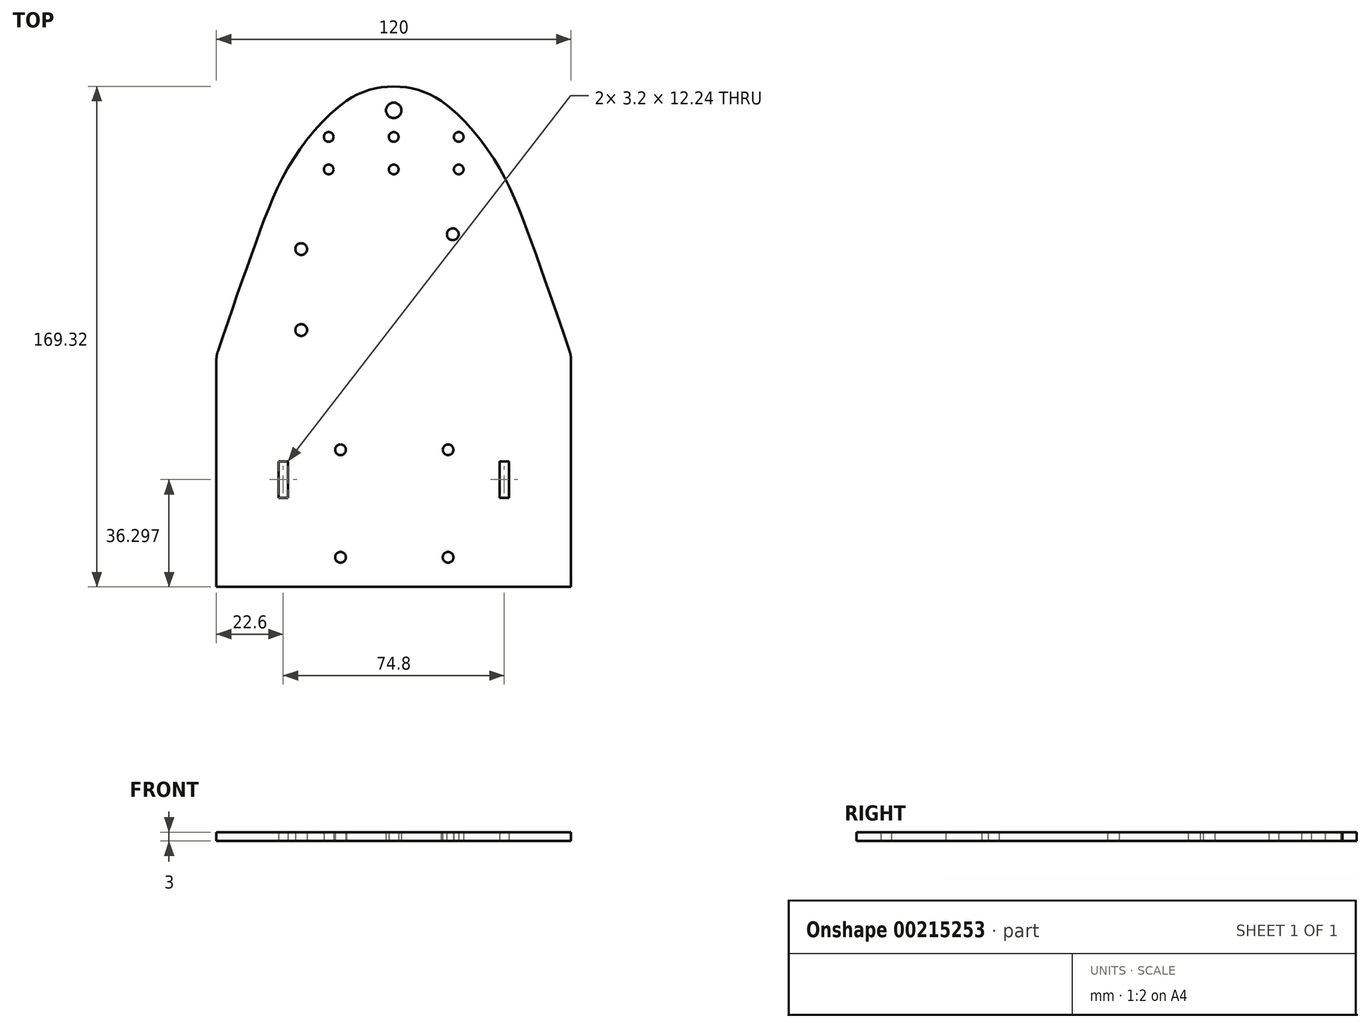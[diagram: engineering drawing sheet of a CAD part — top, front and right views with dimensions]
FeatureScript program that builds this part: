
annotation { "Feature Type Name" : "Feature", "Feature Type Description" : "" }
export const myFeature = defineFeature(function(context is Context, id is Id, definition is map)
    precondition{}
    {
        {
            var Q0;
            Q0=qCreatedBy(makeId("Top.planeOp"),FACE);
            var sketch = newSketch(context, id + "F0", { "sketchPlane" : qUnion([Q0])});
            skLineSegment(sketch, "E0", {"start": v(-69.46, 31.93) * mm, "end": v(50.54, 31.93) * mm, "construction": true});
            skLineSegment(sketch, "E1.bottom", {"start": v(-48.46, 5.05) * mm, "end": v(-45.26, 5.05) * mm});
            skLineSegment(sketch, "E1.top", {"start": v(-48.46, -7.2) * mm, "end": v(-45.26, -7.2) * mm});
            skLineSegment(sketch, "E1.left", {"start": v(-48.46, 5.05) * mm, "end": v(-48.46, -7.2) * mm});
            skLineSegment(sketch, "E1.right", {"start": v(-45.26, 5.05) * mm, "end": v(-45.26, -7.2) * mm});
            skLineSegment(sketch, "E2", {"start": v(-45.26, -1.07) * mm, "end": v(-45.26, -34.07) * mm, "construction": true});
            skLineSegment(sketch, "E3.top", {"start": v(-69.46, -37.37) * mm, "end": v(50.54, -37.37) * mm});
            skLineSegment(sketch, "E3.left", {"start": v(-69.46, 39.35) * mm, "end": v(-69.46, -37.37) * mm});
            skLineSegment(sketch, "E3.right", {"start": v(50.54, 39.35) * mm, "end": v(50.54, -37.37) * mm});
            skLineSegment(sketch, "E4", {"start": v(-45.26, -1.07) * mm, "end": v(-45.26, 31.93) * mm, "construction": true});
            skCircle(sketch, "E5", {"center": v(-27.46, -27.37) * mm, "radius": 1.82 * mm});
            skLineSegment(sketch, "E6", {"start": v(-27.46, -27.37) * mm, "end": v(8.94, -27.37) * mm, "construction": true});
            skCircle(sketch, "E7", {"center": v(8.94, -27.37) * mm, "radius": 1.82 * mm});
            skLineSegment(sketch, "E8", {"start": v(-27.46, -27.37) * mm, "end": v(-27.46, 9.03) * mm, "construction": true});
            skCircle(sketch, "E9", {"center": v(-27.46, 9.03) * mm, "radius": 1.82 * mm});
            skLineSegment(sketch, "E10", {"start": v(-27.46, 9.03) * mm, "end": v(8.94, 9.03) * mm, "construction": true});
            skCircle(sketch, "E11", {"center": v(8.94, 9.03) * mm, "radius": 1.8 * mm});
            skLineSegment(sketch, "E12", {"start": v(-40.76, 81.93) * mm, "end": v(10.54, 81.93) * mm, "construction": true});
            skLineSegment(sketch, "E13", {"start": v(10.54, 81.93) * mm, "end": v(10.54, 76.93) * mm, "construction": true});
            skCircle(sketch, "E14", {"center": v(10.54, 81.93) * mm, "radius": 2 * mm});
            skCircle(sketch, "E15", {"center": v(-40.76, 76.93) * mm, "radius": 2 * mm});
            skLineSegment(sketch, "E16", {"start": v(-40.76, 76.93) * mm, "end": v(-40.76, 49.53) * mm, "construction": true});
            skCircle(sketch, "E17", {"center": v(-40.76, 49.53) * mm, "radius": 2 * mm});
            skLineSegment(sketch, "E18", {"start": v(-40.76, 76.93) * mm, "end": v(-40.76, 81.93) * mm, "construction": true});
            skLineSegment(sketch, "E19", {"start": v(-9.46, -37.37) * mm, "end": v(-9.46, -58.96) * mm, "construction": true});
            skLineSegment(sketch, "E20.MirrorCS", {"start": v(29.54, 5.05) * mm, "end": v(29.54, -7.2) * mm});
            skLineSegment(sketch, "E21.MirrorCS", {"start": v(29.54, 5.05) * mm, "end": v(26.34, 5.05) * mm});
            skLineSegment(sketch, "E22.MirrorCS", {"start": v(29.54, -7.2) * mm, "end": v(26.34, -7.2) * mm});
            skLineSegment(sketch, "E23.MirrorCS", {"start": v(26.34, 5.05) * mm, "end": v(26.34, -7.2) * mm});
            skLineSegment(sketch, "E24", {"start": v(-9.46, 133.88) * mm, "end": v(-9.46, 114.88) * mm, "construction": true});
            skCircle(sketch, "E25", {"center": v(-23.25, 163.1) * mm, "radius": 2 * mm});
            skLineSegment(sketch, "E26", {"start": v(-23.25, 163.1) * mm, "end": v(-23.25, 152.1) * mm, "construction": true});
            skCircle(sketch, "E27", {"center": v(-23.25, 152.1) * mm, "radius": 2 * mm});
            skCircle(sketch, "E28", {"center": v(-9.46, 114.88) * mm, "radius": 1.65 * mm});
            skCircle(sketch, "E29", {"center": v(-9.46, 103.88) * mm, "radius": 1.65 * mm});
            skLineSegment(sketch, "E30", {"start": v(-23.25, 152.1) * mm, "end": v(-38.63, 152.1) * mm, "construction": true});
            skLineSegment(sketch, "E31", {"start": v(-9.46, 114.88) * mm, "end": v(-31.46, 114.88) * mm, "construction": true});
            skCircle(sketch, "E32", {"center": v(-31.46, 114.88) * mm, "radius": 1.65 * mm});
            skCircle(sketch, "E33", {"center": v(-31.46, 103.88) * mm, "radius": 1.65 * mm});
            skCircle(sketch, "E34.MirrorC", {"center": v(12.54, 114.88) * mm, "radius": 1.65 * mm});
            skCircle(sketch, "E35.MirrorC", {"center": v(12.54, 103.88) * mm, "radius": 1.65 * mm});
            skCircle(sketch, "E36", {"center": v(-9.46, 123.88) * mm, "radius": 2.6 * mm});
            skFitSpline(sketch, "E37", {"points": [v(-9.46, 133.88) * mm, v(-25.48, 127.1) * mm, v(-43.56, 107.13) * mm, v(-55.03, 82.17) * mm, v(-69.46, 41.02) * mm], "startDerivative": vector(-81.55, -23.9) * mm, "endDerivative": vector(-48.35, -140.88) * mm});
            skLineSegment(sketch, "E38", {"start": v(-64.44, 55.64) * mm, "end": v(-68.92, 42.6) * mm});
            skFitSpline(sketch, "E39.MirrorCS", {"points": [v(-9.46, 133.88) * mm, v(6.56, 127.1) * mm, v(24.64, 107.13) * mm, v(36.11, 82.17) * mm, v(50.54, 41.02) * mm], "startDerivative": vector(81.55, -23.9) * mm, "endDerivative": vector(48.35, -140.88) * mm});
            skPoint(sketch, "E40.orphan", {"position": v(-69.46, 133.88) * mm});
            skPoint(sketch, "E41.orphan", {"position": v(50.54, 133.88) * mm});
            skArc(sketch, "E42.filletArc", {"start": v(-68.92, 42.6) * mm, "mid": v(-69.32, 41) * mm, "end": v(-69.46, 39.35) * mm});
            skArc(sketch, "E43.filletArc", {"start": v(50.54, 39.35) * mm, "mid": v(50.4, 41) * mm, "end": v(50, 42.6) * mm});
            skArc(sketch, "E44", {"start": v(6.56, 127.1) * mm, "mid": v(-9.46, 131.95) * mm, "end": v(-25.48, 127.1) * mm});
            skLineSegment(sketch, "E45", {"start": v(-9.26, 9.03) * mm, "end": v(-9.26, 92.03) * mm, "construction": true});
            skSolve(sketch);
        }
        {
            var Q0;
            Q0=makeQuery(id+"F0.imprint","IMPRINT",FACE,{"disambiguationData":[TD([[makeQuery(id+"F0.imprint","IMPRINT",EDGE,{"derivedFrom":sQuery(id+"F0.wireOp",EDGE,"E1.bottom")}),1.0]])]});
            extrude(context, id + "F1", {"entities" : qUnion([Q0]), "depth" : 3 * mm});
        }
    });
